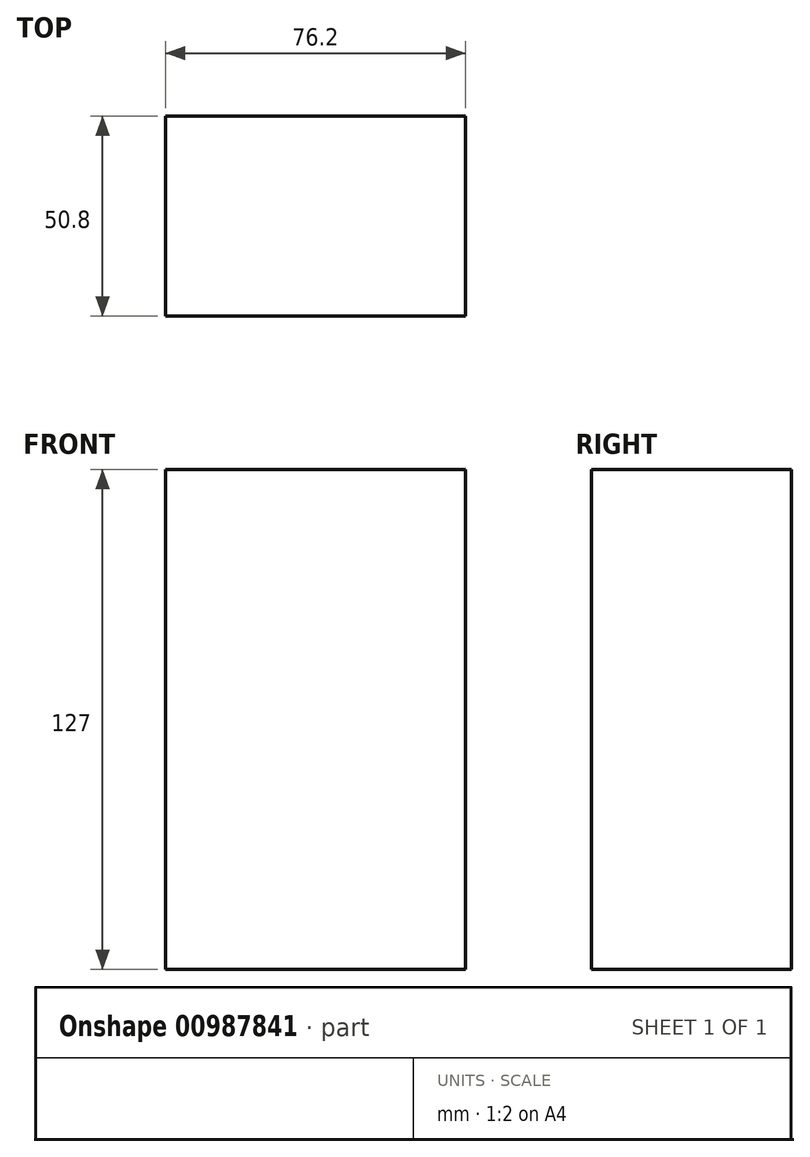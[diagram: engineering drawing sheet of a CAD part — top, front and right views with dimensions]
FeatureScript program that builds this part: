
annotation { "Feature Type Name" : "Feature", "Feature Type Description" : "" }
export const myFeature = defineFeature(function(context is Context, id is Id, definition is map)
    precondition{}
    {
        {
            var Q0;
            Q0=qCreatedBy(makeId("Top.planeOp"),FACE);
            var sketch = newSketch(context, id + "F0", { "sketchPlane" : qUnion([Q0])});
            skLineSegment(sketch, "E0.bottom", {"start": v(-38.1, -25.4) * mm, "end": v(38.1, -25.4) * mm});
            skLineSegment(sketch, "E0.top", {"start": v(-38.1, 25.4) * mm, "end": v(38.1, 25.4) * mm});
            skLineSegment(sketch, "E0.left", {"start": v(-38.1, -25.4) * mm, "end": v(-38.1, 25.4) * mm});
            skLineSegment(sketch, "E0.right", {"start": v(38.1, -25.4) * mm, "end": v(38.1, 25.4) * mm});
            skLineSegment(sketch, "E1", {"start": v(-38.1, 0) * mm, "end": v(38.1, 0) * mm, "construction": true});
            skLineSegment(sketch, "E2", {"start": v(0, 25.4) * mm, "end": v(0, -25.4) * mm, "construction": true});
            skSolve(sketch);
        }
        {
            var Q0;
            Q0 = qSketchRegion(id + "F0", true);
            extrude(context, id + "F1", {"entities" : qUnion([Q0]), "depth" : 127 * mm, "offsetDistance" : 25.4 * mm});
        }
    });
